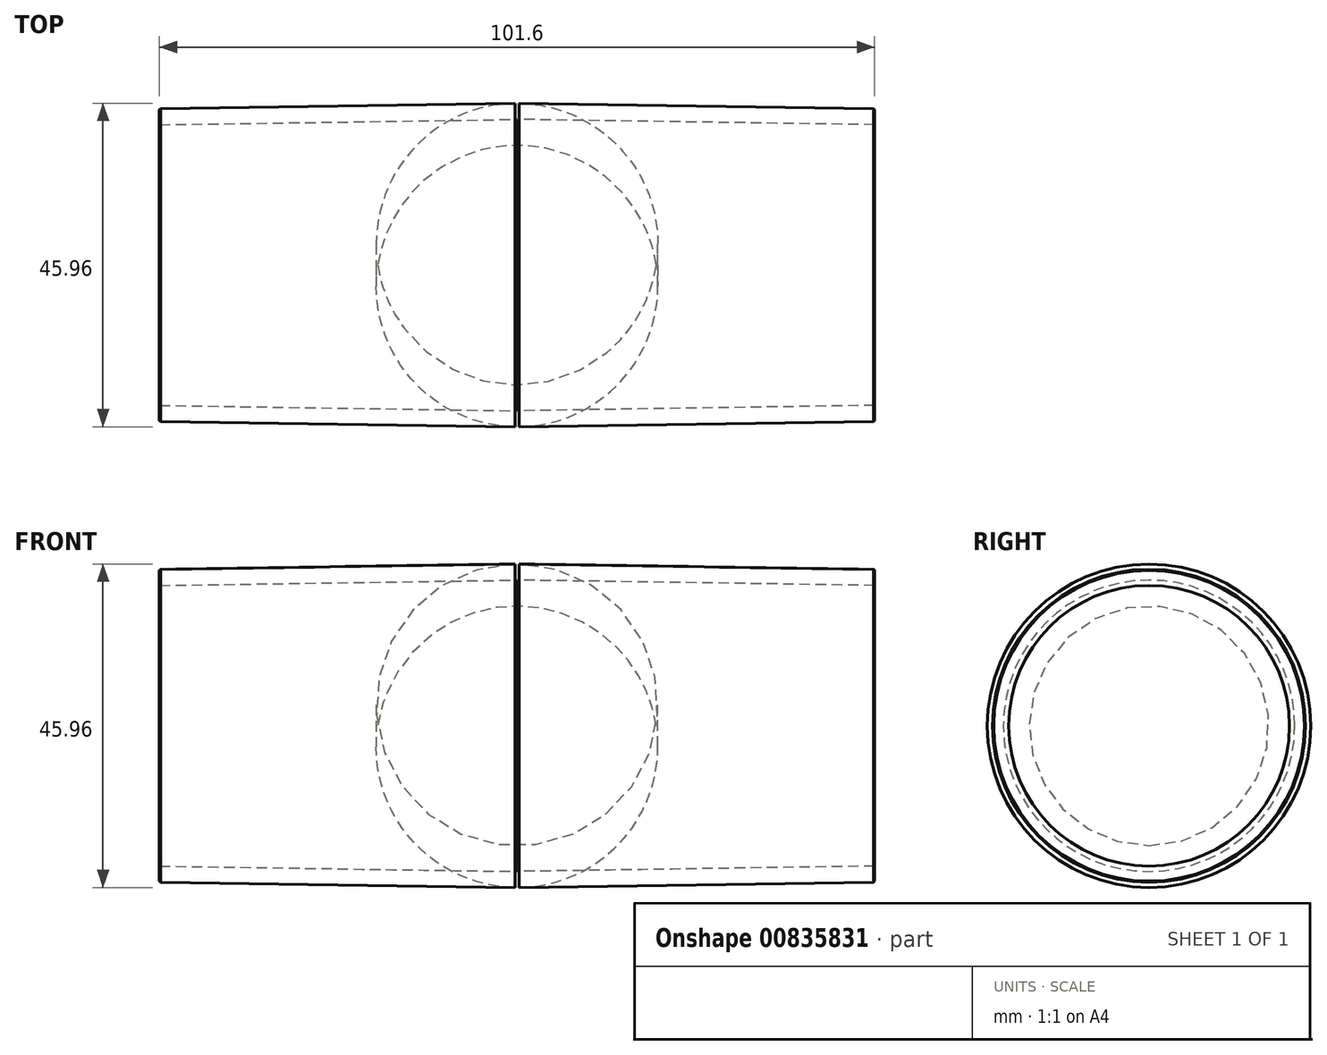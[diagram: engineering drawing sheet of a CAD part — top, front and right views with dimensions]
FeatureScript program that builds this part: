
annotation { "Feature Type Name" : "Feature", "Feature Type Description" : "" }
export const myFeature = defineFeature(function(context is Context, id is Id, definition is map)
    precondition{}
    {
        {
            assignVariable(context, id + "F0", {"name" : "OD_radius", "anyValue" : 20});
        }
        {
            assignVariable(context, id + "F1", {"name" : "chamfer", "anyValue" : .15});
        }
        {
            var Q0;
            Q0=qCreatedBy(makeId("Front.planeOp"),FACE);
            var sketch = newSketch(context, id + "F2", { "sketchPlane" : qUnion([Q0])});
            skLineSegment(sketch, "E0", {"start": v(0, 22.99) * mm, "end": v(50.8, 22.23) * mm});
            skLineSegment(sketch, "E1", {"start": v(0, 0) * mm, "end": v(-86.25, 0) * mm, "construction": true});
            skPoint(sketch, "E2", {"position": v(25.4, 22.6) * mm});
            skLineSegment(sketch, "E3", {"start": v(0, 22.99) * mm, "end": v(0, 20.7) * mm});
            skLineSegment(sketch, "E4", {"start": v(0, 20.7) * mm, "end": v(50.8, 19.94) * mm});
            skLineSegment(sketch, "E5", {"start": v(50.8, 19.94) * mm, "end": v(50.8, 22.23) * mm});
            skSolve(sketch);
        }
        {
            var Q0;
            Q0 = qSketchRegion(id + "F2", true);
            var Q1;
            Q1=sQuery(id+"F2.wireOp",EDGE,"E1");
            revolve(context, id + "F3", {"surfaceOperationType" : NewSurfaceOperationType.NEW, "entities" : qUnion([Q0]), "axis" : qUnion([Q1]), "revolveType" : RevolveType.FULL});
        }
        {
            var Q0;
            Q0=makeQuery(id+"F3.opRevolve","SWEPT_BODY",BODY,{"disambiguationData":[OSD([sQuery(id+"F2.wireOp",EDGE,"E0"),sQuery(id+"F2.wireOp",EDGE,"E3"),sQuery(id+"F2.wireOp",EDGE,"E4"),sQuery(id+"F2.wireOp",EDGE,"E5")])]});
            var Q1;
            Q1=makeQuery(id+"F3.opRevolve","SWEPT_FACE",FACE,{"disambiguationData":[OSD([sQuery(id+"F2.wireOp",EDGE,"E3")])]});
            mirror(context, id + "F4", {"operationType" : NewBodyOperationType.ADD, "entities" : qUnion([Q0]), "mirrorPlane" : qUnion([Q1])});
        }
        {
            var Q0;
            {var subQ0=makeQuery(id+"F3.opRevolve","SWEPT_EDGE",EDGE,{"disambiguationData":[OSD([sQuery(id+"F2.wireOp",EDGE,"E0"),sQuery(id+"F2.wireOp",EDGE,"E3")])]});Q0=makeQuery(id+"F4.boolean.opBoolean","MERGE",EDGE,{"derivedFrom":[subQ0,makeQuery(id+"F4.opPattern","COPY",EDGE,{"derivedFrom":subQ0,"instanceName":"1"})]});}
            fillet(context, id + "F5", {"entities" : qUnion([Q0]), "radius" : (getVariable(context, 'OD_radius')) * mm, "tangentPropagation" : true, "allowEdgeOverflow" : false});
        }
        {
            var Q0;
            Q0=makeQuery(id+"F4.opPattern","COPY",EDGE,{"derivedFrom":makeQuery(id+"F3.opRevolve","SWEPT_EDGE",EDGE,{"disambiguationData":[OSD([sQuery(id+"F2.wireOp",EDGE,"E0"),sQuery(id+"F2.wireOp",EDGE,"E5")])]}),"instanceName":"1"});
            var Q1;
            Q1=makeQuery(id+"F3.opRevolve","SWEPT_EDGE",EDGE,{"disambiguationData":[OSD([sQuery(id+"F2.wireOp",EDGE,"E0"),sQuery(id+"F2.wireOp",EDGE,"E5")])]});
            chamfer(context, id + "F6", {"entities" : qUnion([Q0, Q1]), "width" : (getVariable(context, 'chamfer')) * mm, "tangentPropagation" : true});
        }
    });
